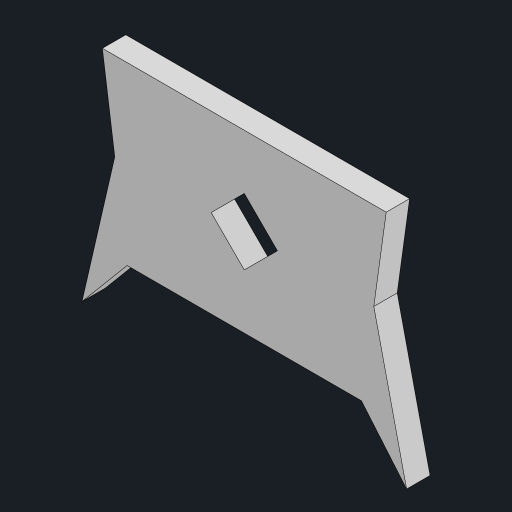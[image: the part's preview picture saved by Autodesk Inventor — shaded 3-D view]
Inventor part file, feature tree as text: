
AUTODESK INVENTOR PART (.ipt)
format: ipt  version: 2023 (Build 270158000, 158)  size: 115,712 bytes
history: native  units: mm
features: extrude x2, sketch x2, other x1, mirror x1, projected_geometry x1
ambient origin geometry x8: Origin, YZ Plane, XZ Plane, XY Plane, X Axis, Y Axis, Z Axis, Center Point
bodies: Body1 (feature_tree)
feature tree (7):
  other  "ソリッド1"
  extrude  "押し出し1"  Depth=2.0mm TaperAngle=0.0deg
  extrude  "押し出し2"  Depth=6.0mm
  mirror  "ミラー1"
  sketch  "スケッチ1"
  sketch  "スケッチ2"
  projected_geometry  "投影ループ1"
